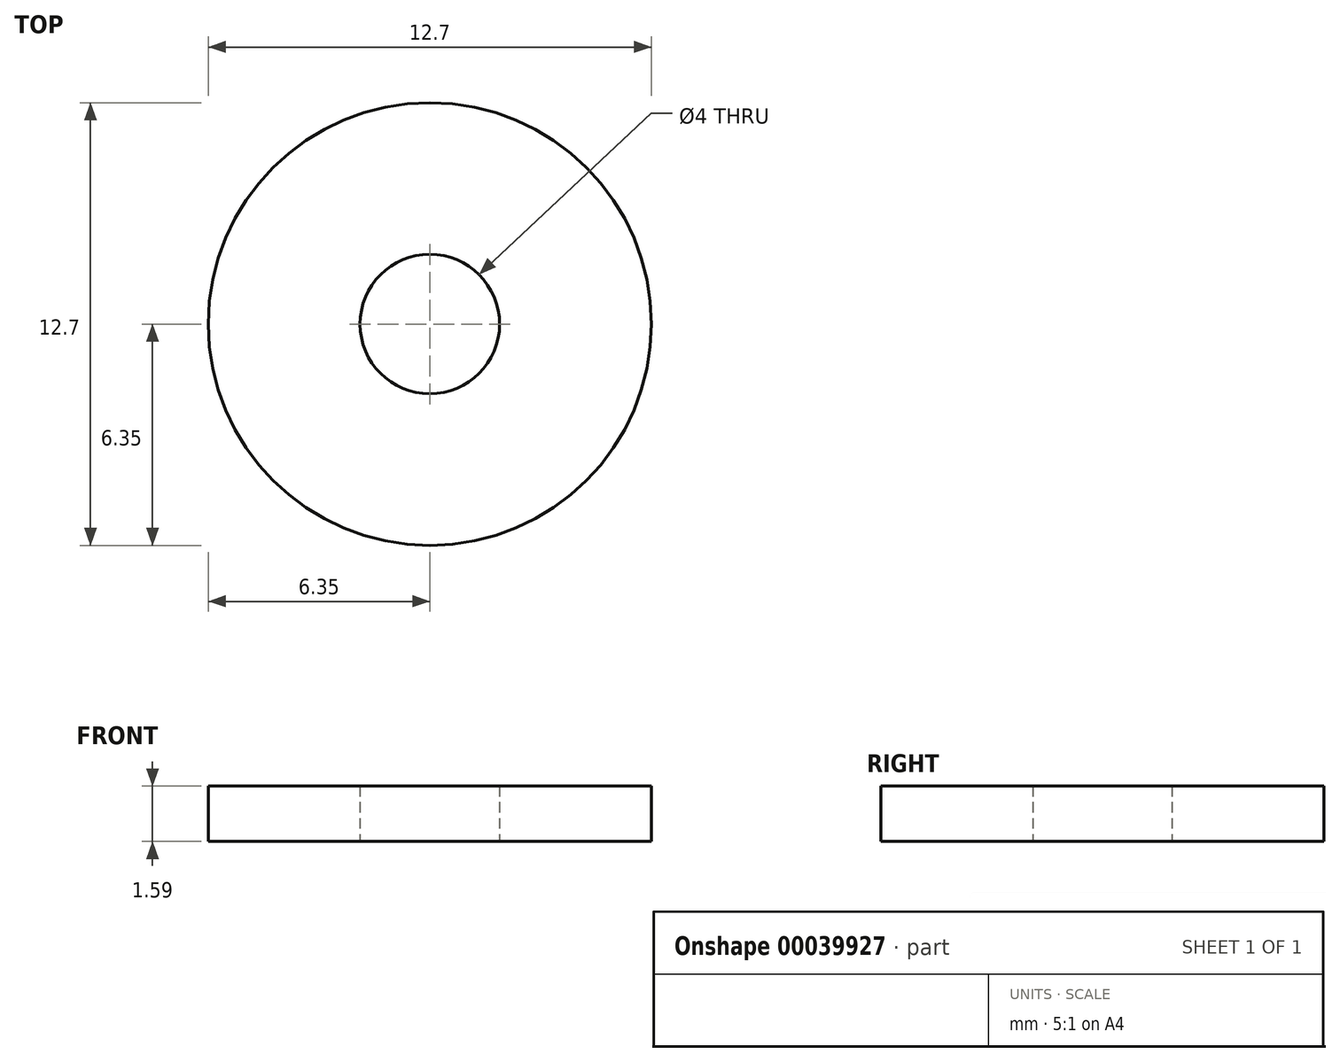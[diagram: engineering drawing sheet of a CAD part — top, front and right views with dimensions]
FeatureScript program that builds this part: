
annotation { "Feature Type Name" : "Feature", "Feature Type Description" : "" }
export const myFeature = defineFeature(function(context is Context, id is Id, definition is map)
    precondition{}
    {
        {
            var Q0;
            Q0=qCreatedBy(makeId("Top.planeOp"),FACE);
            var sketch = newSketch(context, id + "F0", { "sketchPlane" : qUnion([Q0])});
            skCircle(sketch, "E0", {"center": v(0, 0) * mm, "radius": 2 * mm});
            skCircle(sketch, "E1", {"center": v(0, 0) * mm, "radius": 6.35 * mm});
            skSolve(sketch);
        }
        {
            var Q0;
            Q0=makeQuery(id+"F0.imprint","IMPRINT",FACE,{"disambiguationData":[TD([[makeQuery(id+"F0.imprint","IMPRINT",EDGE,{"derivedFrom":sQuery(id+"F0.wireOp",EDGE,"E0")}),-1.0]])]});
            extrude(context, id + "F1", {"entities" : qUnion([Q0]), "depth" : 1.59 * mm});
        }
    });
